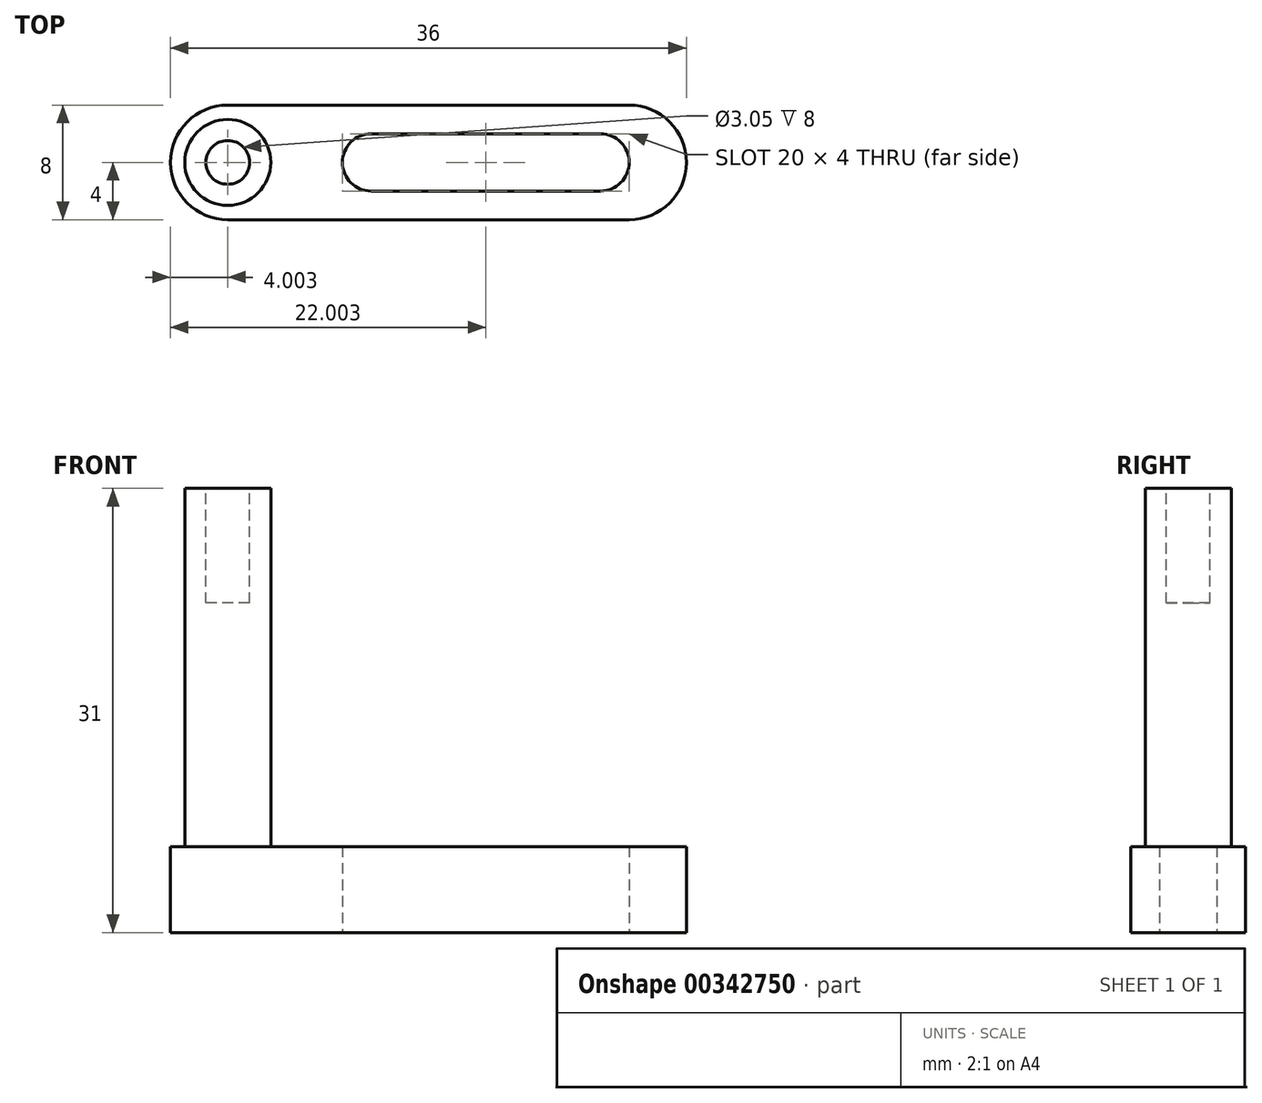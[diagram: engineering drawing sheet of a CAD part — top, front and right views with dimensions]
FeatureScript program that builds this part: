
annotation { "Feature Type Name" : "Feature", "Feature Type Description" : "" }
export const myFeature = defineFeature(function(context is Context, id is Id, definition is map)
    precondition{}
    {
        {
            var Q0;
            Q0=qCreatedBy(makeId("Top.planeOp"),FACE);
            var sketch = newSketch(context, id + "F0", { "sketchPlane" : qUnion([Q0])});
            skLineSegment(sketch, "E0", {"start": v(-56.74, 4) * mm, "end": v(-28.74, 4) * mm});
            skArc(sketch, "E1", {"start": v(-28.74, 4) * mm, "mid": v(-25.9, 2.83) * mm, "end": v(-24.74, 0) * mm});
            skLineSegment(sketch, "E2", {"start": v(-46.74, 2) * mm, "end": v(-30.74, 2) * mm});
            skArc(sketch, "E3", {"start": v(-48.74, 0) * mm, "mid": v(-48.15, 1.41) * mm, "end": v(-46.74, 2) * mm});
            skArc(sketch, "E4", {"start": v(-28.74, 0) * mm, "mid": v(-29.32, 1.41) * mm, "end": v(-30.74, 2) * mm});
            skArc(sketch, "E5", {"start": v(-56.74, 4) * mm, "mid": v(-59.57, 2.83) * mm, "end": v(-60.74, 0) * mm});
            skArc(sketch, "E6.MirrorCS", {"start": v(-56.74, -4) * mm, "mid": v(-59.57, -2.83) * mm, "end": v(-60.74, 0) * mm});
            skLineSegment(sketch, "E7.MirrorCS", {"start": v(-56.74, -4) * mm, "end": v(-28.74, -4) * mm});
            skArc(sketch, "E8.MirrorCS", {"start": v(-28.74, -4) * mm, "mid": v(-25.9, -2.83) * mm, "end": v(-24.74, 0) * mm});
            skArc(sketch, "E9.MirrorCS", {"start": v(-28.74, 0) * mm, "mid": v(-29.32, -1.41) * mm, "end": v(-30.74, -2) * mm});
            skLineSegment(sketch, "E10.MirrorCS", {"start": v(-46.74, -2) * mm, "end": v(-30.74, -2) * mm});
            skArc(sketch, "E11.MirrorCS", {"start": v(-48.74, 0) * mm, "mid": v(-48.15, -1.41) * mm, "end": v(-46.74, -2) * mm});
            skSolve(sketch);
        }
        {
            var Q0;
            Q0=makeQuery(id+"F0.imprint","IMPRINT",FACE,{"disambiguationData":[TD([[makeQuery(id+"F0.imprint","IMPRINT",EDGE,{"derivedFrom":sQuery(id+"F0.wireOp",EDGE,"E0")}),-1.0]])]});
            extrude(context, id + "F1", {"entities" : qUnion([Q0]), "depth" : 6 * mm});
        }
        {
            var Q0;
            Q0=makeQuery(id+"F1.opExtrude","CAP_FACE",FACE,{"disambiguationData":[OSD([sQuery(id+"F0.wireOp",EDGE,"E0"),sQuery(id+"F0.wireOp",EDGE,"E1"),sQuery(id+"F0.wireOp",EDGE,"E2"),sQuery(id+"F0.wireOp",EDGE,"E3"),sQuery(id+"F0.wireOp",EDGE,"E4"),sQuery(id+"F0.wireOp",EDGE,"E5"),sQuery(id+"F0.wireOp",EDGE,"E6.MirrorCS"),sQuery(id+"F0.wireOp",EDGE,"E7.MirrorCS"),sQuery(id+"F0.wireOp",EDGE,"E8.MirrorCS"),sQuery(id+"F0.wireOp",EDGE,"E9.MirrorCS"),sQuery(id+"F0.wireOp",EDGE,"E10.MirrorCS"),sQuery(id+"F0.wireOp",EDGE,"E11.MirrorCS")])],"isStart":false});
            var sketch = newSketch(context, id + "F2", { "sketchPlane" : qUnion([Q0])});
            skCircle(sketch, "E12", {"center": v(-56.74, 0) * mm, "radius": 3 * mm});
            skSolve(sketch);
        }
        {
            var Q0;
            Q0=makeQuery(id+"F2.imprint","IMPRINT",FACE,{"disambiguationData":[TD([[makeQuery(id+"F2.imprint","IMPRINT",EDGE,{"derivedFrom":sQuery(id+"F2.wireOp",EDGE,"E12")}),1.0]])]});
            extrude(context, id + "F3", {"entities" : qUnion([Q0]), "operationType" : NewBodyOperationType.ADD, "depth" : 25 * mm});
        }
        {
            var Q0;
            Q0=makeQuery(id+"F3.opExtrude","CAP_FACE",FACE,{"disambiguationData":[OSD([sQuery(id+"F2.wireOp",EDGE,"E12")])],"isStart":false});
            var sketch = newSketch(context, id + "F4", { "sketchPlane" : qUnion([Q0])});
            skCircle(sketch, "E13", {"center": v(-56.74, 0) * mm, "radius": 1.52 * mm});
            skSolve(sketch);
        }
        {
            var Q0;
            Q0=makeQuery(id+"F4.imprint","IMPRINT",FACE,{"disambiguationData":[TD([[makeQuery(id+"F4.imprint","IMPRINT",EDGE,{"derivedFrom":sQuery(id+"F4.wireOp",EDGE,"E13")}),1.0]])]});
            extrude(context, id + "F5", {"entities" : qUnion([Q0]), "operationType" : NewBodyOperationType.REMOVE, "oppositeDirection" : true, "depth" : 8 * mm});
        }
    });
